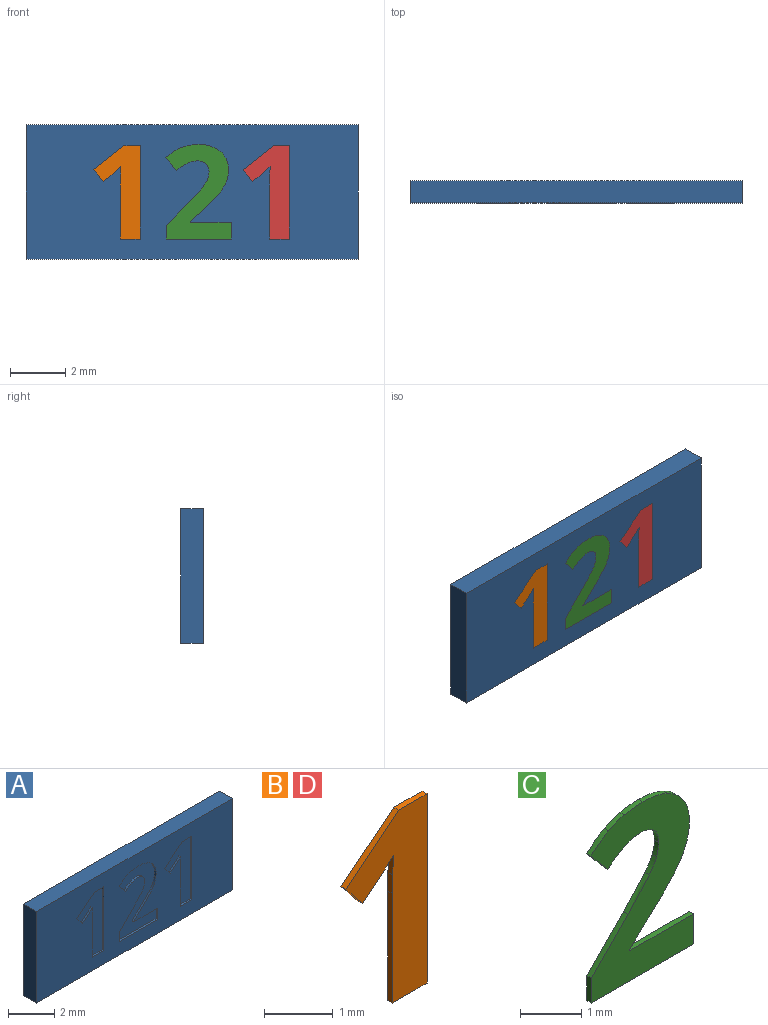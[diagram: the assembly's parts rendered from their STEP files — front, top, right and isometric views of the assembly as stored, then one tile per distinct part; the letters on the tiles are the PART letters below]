
ASSEMBLY  parts=4 mates=3
PART A: 53 faces, bbox 12x0.8x4.9 mm
  f0: plane 12x4.85mm, normal (0,-1,0), area 48.1mm2, adj f1,f2,f3,f4,f6,f7,f8,f9
  f1: plane 4.85x0.8mm, normal (1,0,0), area 3.9mm2, adj f0,f2,f4,f5
  f2: plane 12x0.8mm, normal (0,0,1), area 9.6mm2, adj f0,f1,f3,f5
  f3: plane 4.85x0.8mm, normal (-1,0,0), area 3.9mm2, adj f0,f2,f4,f5
  f4: plane 12x0.8mm, normal (0,0,-1), area 9.6mm2, adj f0,f1,f3,f5
  f5: plane 12x4.85mm, normal (0,1,0), area 58.2mm2, adj f1,f2,f3,f4
  f6: plane 3.37x0.1mm, normal (-1,0,0), area 0.3mm2, adj f0,f7,f15,f16
  f7: plane 0.59x0.1mm, normal (0,0,-1), area 0.1mm2, adj f0,f6,f8,f16
  f8: plane 1.09x0.86mm, normal (0.62,0,-0.78), area 0.1mm2, adj f0,f7,f9,f16
  f9: plane 0.43x0.34mm, normal (0.78,0,0.63), area 0.1mm2, adj f0,f8,f10,f16
  f10: plane 0.39x0.31mm, normal (-0.63,0,0.78), area 0mm2, adj f0,f9,f11,f16
  f11: extruded ~0.25x0.23mm, area 0mm2, adj f0,f10,f12,f16
  f12: plane 0.35x0.1mm, normal (1,0,-0.03), area 0mm2, adj f0,f11,f13,f16
  f13: plane 0.32x0.1mm, normal (1,0,-0.02), area 0mm2, adj f0,f12,f14,f16
  f14: plane 1.95x0.1mm, normal (1,0,0), area 0.2mm2, adj f0,f13,f15,f16
  f15: plane 0.71x0.1mm, normal (0,0,1), area 0.1mm2, adj f0,f6,f14,f16
  f16: plane 3.37x1.67mm, normal (0,-1,0), area 2.9mm2, adj f6,f7,f8,f9,f10,f11,f12,f13
  f17: plane 0.6x0.1mm, normal (-1,0,0), area 0.1mm2, adj f0,f18,f40,f41
  f18: plane 1.47x0.1mm, normal (0,0,-1), area 0.1mm2, adj f0,f17,f19,f41
  f19: plane 0.1x0.03mm, normal (-1,0,0), area 0mm2, adj f0,f18,f20,f41
  f20: plane 0.43x0.41mm, normal (-0.69,0,0.73), area 0.1mm2, adj f0,f19,f21,f41
  f21: extruded ~0.61x0.61mm, area 0.1mm2, adj f0,f20,f22,f41
  f22: extruded ~0.42x0.25mm, area 0mm2, adj f0,f21,f23,f41
  f23: extruded ~0.44x0.1mm, area 0mm2, adj f0,f22,f24,f41
  f24: extruded ~0.48x0.13mm, area 0.1mm2, adj f0,f23,f25,f41
  f25: extruded ~0.38x0.32mm, area 0.1mm2, adj f0,f24,f26,f41
  f26: extruded ~0.56x0.12mm, area 0.1mm2, adj f0,f25,f27,f41
  f27: extruded ~0.43x0.1mm, area 0mm2, adj f0,f26,f28,f41
  f28: extruded ~0.36x0.13mm, area 0mm2, adj f0,f27,f29,f41
  f29: extruded ~0.41x0.3mm, area 0.1mm2, adj f0,f28,f30,f41
  f30: plane 0.46x0.39mm, normal (0.76,0,0.65), area 0.1mm2, adj f0,f29,f31,f41
  f31: extruded ~0.39x0.26mm, area 0mm2, adj f0,f30,f32,f41
  f32: extruded ~0.38x0.1mm, area 0mm2, adj f0,f31,f33,f41
  f33: extruded ~0.3x0.1mm, area 0mm2, adj f0,f32,f34,f41
  f34: extruded ~0.3x0.11mm, area 0mm2, adj f0,f33,f35,f41
  f35: extruded ~0.26x0.1mm, area 0mm2, adj f0,f34,f36,f41
  f36: extruded ~0.28x0.17mm, area 0mm2, adj f0,f35,f37,f41
  f37: extruded ~0.53x0.49mm, area 0.1mm2, adj f0,f36,f38,f41
  f38: plane 0.86x0.85mm, normal (0.71,0,-0.7), area 0.1mm2, adj f0,f37,f39,f41
  f39: plane 0.5x0.1mm, normal (1,0,0), area 0mm2, adj f0,f38,f40,f41
  f40: plane 2.36x0.1mm, normal (0,0,1), area 0.2mm2, adj f0,f17,f39,f41
  f41: plane 3.42x2.37mm, normal (0,-1,0), area 4.2mm2, adj f17,f18,f19,f20,f21,f22,f23,f24
  f42: plane 3.37x0.1mm, normal (-1,0,0), area 0.3mm2, adj f0,f43,f51,f52
  f43: plane 0.59x0.1mm, normal (0,0,-1), area 0.1mm2, adj f0,f42,f44,f52
  f44: plane 1.09x0.86mm, normal (0.62,0,-0.78), area 0.1mm2, adj f0,f43,f45,f52
  f45: plane 0.43x0.34mm, normal (0.78,0,0.63), area 0.1mm2, adj f0,f44,f46,f52
  f46: plane 0.39x0.31mm, normal (-0.63,0,0.78), area 0mm2, adj f0,f45,f47,f52
  f47: extruded ~0.25x0.23mm, area 0mm2, adj f0,f46,f48,f52
  f48: plane 0.35x0.1mm, normal (1,0,-0.03), area 0mm2, adj f0,f47,f49,f52
  f49: plane 0.32x0.1mm, normal (1,0,-0.02), area 0mm2, adj f0,f48,f50,f52
  f50: plane 1.95x0.1mm, normal (1,0,0), area 0.2mm2, adj f0,f49,f51,f52
  f51: plane 0.71x0.1mm, normal (0,0,1), area 0.1mm2, adj f0,f42,f50,f52
  f52: plane 3.37x1.67mm, normal (0,-1,0), area 2.9mm2, adj f42,f43,f44,f45,f46,f47,f48,f49
PART B: 12 faces, bbox 1.7x0.1x3.4 mm
  f0: plane 3.37x1.67mm, normal (0,-1,0), area 2.9mm2, adj f1,f2,f3,f4,f5,f6,f7,f9
  f1: plane 0.59x0.1mm, normal (0,0,1), area 0.1mm2, adj f0,f2,f8,f10
  f2: plane 1.09x0.86mm, normal (-0.62,0,0.78), area 0.1mm2, adj f0,f1,f3,f8
  f3: plane 0.43x0.34mm, normal (-0.78,0,-0.63), area 0.1mm2, adj f0,f2,f4,f8
  f4: plane 0.39x0.31mm, normal (0.63,0,-0.78), area 0mm2, adj f0,f3,f5,f8
  f5: extruded ~0.25x0.23mm, area 0mm2, adj f0,f4,f6,f8
  f6: plane 0.35x0.1mm, normal (-1,0,0.03), area 0mm2, adj f0,f5,f7,f8
  f7: plane 0.32x0.1mm, normal (-1,0,0.02), area 0mm2, adj f0,f6,f8,f9
  f8: plane 3.37x1.67mm, normal (0,1,0), area 2.9mm2, adj f1,f2,f3,f4,f5,f6,f7,f9
  f9: plane 1.95x0.1mm, normal (-1,0,0), area 0.2mm2, adj f0,f7,f8,f11
  f10: plane 3.37x0.1mm, normal (1,0,0), area 0.3mm2, adj f0,f1,f8,f11
  f11: plane 0.71x0.1mm, normal (0,0,-1), area 0.1mm2, adj f0,f8,f9,f10
PART C: 26 faces, bbox 2.4x0.1x3.4 mm
  f0: plane 3.42x2.37mm, normal (0,-1,0), area 4.2mm2, adj f1,f2,f3,f4,f5,f6,f7,f8
  f1: plane 1.47x0.1mm, normal (0,0,1), area 0.1mm2, adj f0,f2,f22,f24
  f2: plane 0.1x0.03mm, normal (1,0,0), area 0mm2, adj f0,f1,f3,f22
  f3: plane 0.43x0.41mm, normal (0.69,0,-0.73), area 0.1mm2, adj f0,f2,f4,f22
  f4: extruded ~0.61x0.61mm, area 0.1mm2, adj f0,f3,f5,f22
  f5: extruded ~0.42x0.25mm, area 0mm2, adj f0,f4,f6,f22
  f6: extruded ~0.44x0.1mm, area 0mm2, adj f0,f5,f7,f22
  f7: extruded ~0.48x0.13mm, area 0.1mm2, adj f0,f6,f8,f22
  f8: extruded ~0.38x0.32mm, area 0.1mm2, adj f0,f7,f9,f22
  f9: extruded ~0.56x0.12mm, area 0.1mm2, adj f0,f8,f10,f22
  f10: extruded ~0.43x0.1mm, area 0mm2, adj f0,f9,f11,f22
  f11: extruded ~0.36x0.13mm, area 0mm2, adj f0,f10,f12,f22
  f12: extruded ~0.41x0.3mm, area 0.1mm2, adj f0,f11,f13,f22
  f13: plane 0.46x0.39mm, normal (-0.76,0,-0.65), area 0.1mm2, adj f0,f12,f14,f22
  f14: extruded ~0.39x0.26mm, area 0mm2, adj f0,f13,f15,f22
  f15: extruded ~0.38x0.1mm, area 0mm2, adj f0,f14,f16,f22
  f16: extruded ~0.3x0.1mm, area 0mm2, adj f0,f15,f17,f22
  f17: extruded ~0.3x0.11mm, area 0mm2, adj f0,f16,f18,f22
  f18: extruded ~0.26x0.1mm, area 0mm2, adj f0,f17,f19,f22
  f19: extruded ~0.28x0.17mm, area 0mm2, adj f0,f18,f20,f22
  f20: extruded ~0.53x0.49mm, area 0.1mm2, adj f0,f19,f21,f22
  f21: plane 0.86x0.85mm, normal (-0.71,0,0.7), area 0.1mm2, adj f0,f20,f22,f23
  f22: plane 3.42x2.37mm, normal (0,1,0), area 4.2mm2, adj f1,f2,f3,f4,f5,f6,f7,f8
  f23: plane 0.5x0.1mm, normal (-1,0,0), area 0mm2, adj f0,f21,f22,f25
  f24: plane 0.6x0.1mm, normal (1,0,0), area 0.1mm2, adj f0,f1,f22,f25
  f25: plane 2.36x0.1mm, normal (0,0,-1), area 0.2mm2, adj f0,f22,f23,f24
PART D: same geometry as B
PLACE A t=(-0.02,0.37,-0.03)mm
PLACE B t=(-4.29,0.37,-0.03)mm
PLACE C t=(-1.29,0.37,-0.03)mm
PLACE D t=(1.1,0.37,-0.03)mm
MATE fastened B.f0 <-> A.f0  axis (0,-1,0) through (-2.61,-0.43,-1.73)mm
MATE fastened D.f0 <-> A.f0  axis (0,-1,0) through (2.78,-0.43,-1.73)mm
MATE fastened C.f0 <-> A.f0  axis (0,-1,0) through (-0.96,-0.43,-1.73)mm
